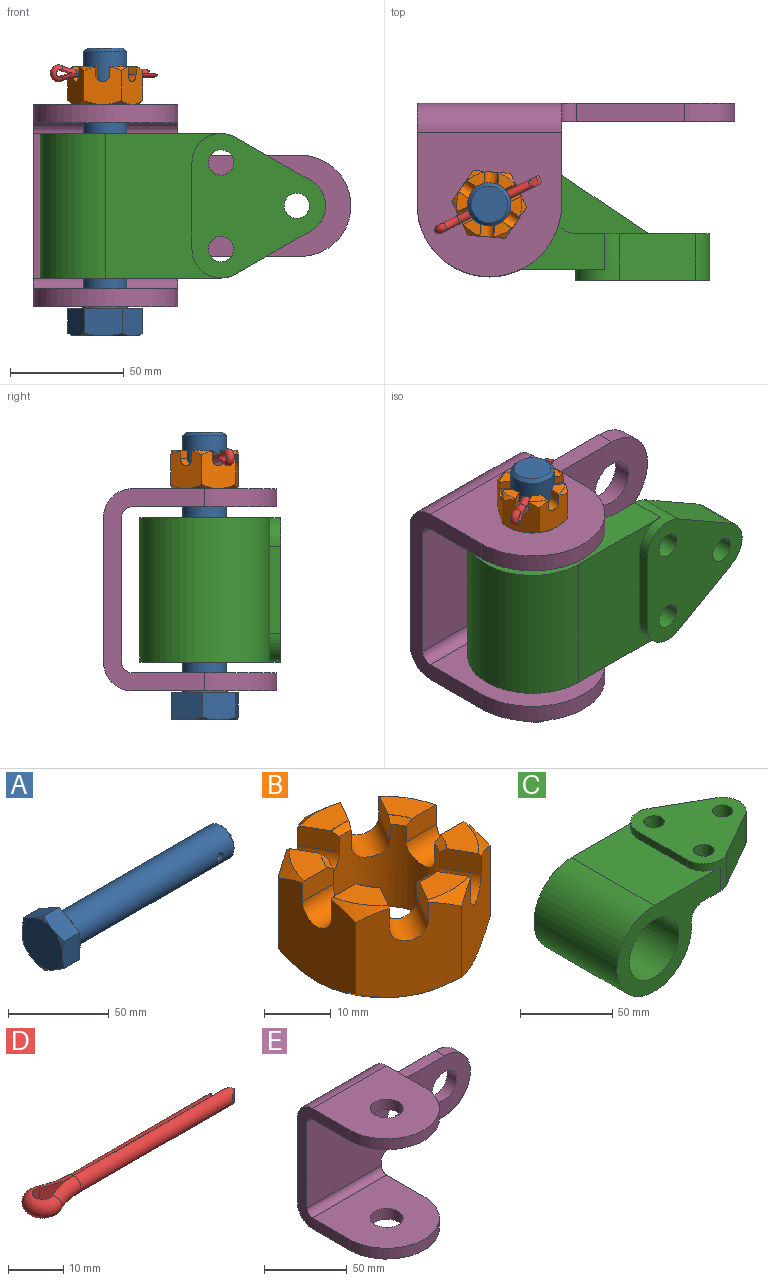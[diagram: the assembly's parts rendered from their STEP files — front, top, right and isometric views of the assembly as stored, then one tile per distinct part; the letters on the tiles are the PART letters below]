
ASSEMBLY  parts=5 mates=4
PART A: 26 faces, bbox 126.6x33x33 mm
  f0: plane 28.58x28.58mm, normal (1,0,0), area 325.1mm2, adj f10,f24
  f1: cylinder r=9.53mm len=112.28mm, axis (-1,0,0), area 6683.8mm2, adj f2,f24,f25
  f2: cone r=8.01mm half-angle=45deg, axis (-1,0,0), area 117.9mm2, adj f1,f3
  f3: plane 16.03x16.03mm, normal (1,0,0), area 201.7mm2, adj f2
  f4: plane 12.37x7.14mm, normal (1,0,0), area 11mm2, adj f10,f18,f23
  f5: plane 14.29x4.12mm, normal (1,0,0), area 11mm2, adj f10,f22,f23
  f6: plane 12.37x7.14mm, normal (1,0,0), area 11mm2, adj f10,f21,f22
  f7: plane 12.37x7.14mm, normal (1,0,0), area 11mm2, adj f10,f20,f21
  f8: plane 14.29x4.12mm, normal (1,0,0), area 11mm2, adj f10,f19,f20
  f9: plane 12.37x7.14mm, normal (1,0,0), area 11mm2, adj f10,f18,f19
  f10: cylinder r=14.29mm len=28.58mm, axis (-1,0,0), area 34.2mm2, adj f0,f4,f5,f6,f7,f8,f9
  f11: plane 28.58x28.58mm, normal (-1,0,0), area 641.3mm2, adj f12,f13,f14,f15,f16,f17
  f12: cone r=14.29mm half-angle=60deg, axis (1,0,0), area 12.7mm2, adj f11,f22,f23
  f13: cone r=14.29mm half-angle=60deg, axis (1,0,0), area 12.7mm2, adj f11,f21,f22
  f14: cone r=14.29mm half-angle=60deg, axis (1,0,0), area 12.7mm2, adj f11,f20,f21
  f15: cone r=14.29mm half-angle=60deg, axis (1,0,0), area 12.7mm2, adj f11,f19,f20
  f16: cone r=14.29mm half-angle=60deg, axis (1,0,0), area 12.7mm2, adj f11,f18,f23
  f17: cone r=14.29mm half-angle=60deg, axis (1,0,0), area 12.7mm2, adj f11,f18,f19
  f18: plane 16.51x11.89mm, normal (0,1,0), area 188.9mm2, adj f4,f9,f16,f17,f19,f23
  f19: plane 14.29x11.89mm, normal (0,0.5,-0.87), area 188.9mm2, adj f8,f9,f15,f17,f18,f20
  f20: plane 14.29x11.89mm, normal (0,-0.5,-0.87), area 188.9mm2, adj f7,f8,f14,f15,f19,f21
  f21: plane 16.51x11.89mm, normal (0,-1,0), area 188.9mm2, adj f6,f7,f13,f14,f20,f22
  f22: plane 14.29x11.89mm, normal (0,-0.5,0.87), area 188.9mm2, adj f5,f6,f12,f13,f21,f23
  f23: plane 14.29x11.89mm, normal (0,0.5,0.87), area 188.9mm2, adj f4,f5,f12,f16,f18,f22
  f24: torus R=10.03mm, axis (1,0,0), area 48.7mm2, adj f0,f1
  f25: cylinder r=2.38mm len=19.05mm, axis (0,-1,0), area 285mm2, adj f1
PART B: 64 faces, bbox 33x33x16.9 mm
  f0: cylinder r=8.33mm len=16.67mm, axis (0,0,1), area 599.6mm2, adj f8,f9,f10,f11,f12,f13,f14,f15
  f1: plane 28.58x28.58mm, normal (0,0,-1), area 356.3mm2, adj f32,f33,f34,f35,f36,f37,f51
  f2: plane 8.68x4.95mm, normal (0,0,1), area 30mm2, adj f12,f16,f41,f48
  f3: plane 7.52x6.81mm, normal (0,0,1), area 30mm2, adj f9,f13,f43,f49
  f4: plane 7.52x6.81mm, normal (0,0,1), area 30mm2, adj f8,f18,f39,f44
  f5: plane 7.52x6.81mm, normal (0,0,1), area 30mm2, adj f11,f15,f42,f46
  f6: plane 7.52x6.81mm, normal (0,0,1), area 30mm2, adj f10,f17,f40,f47
  f7: plane 8.68x4.95mm, normal (0,0,1), area 30mm2, adj f14,f19,f38,f45
  f8: plane 6.56x3.71mm, normal (0,-1,0), area 23.4mm2, adj f0,f4,f22,f26,f39,f44,f62,f63
  f9: plane 6.56x3.71mm, normal (0,1,0), area 23.4mm2, adj f0,f3,f22,f26,f43,f49,f52,f53
  f10: plane 6.56x3.71mm, normal (0,1,0), area 23.4mm2, adj f0,f6,f25,f27,f40,f47,f56,f57
  f11: plane 6.56x3.71mm, normal (0,-1,0), area 23.4mm2, adj f0,f5,f25,f27,f42,f46,f58,f59
  f12: plane 5.69x3.71mm, normal (0.87,0.5,0), area 23.4mm2, adj f0,f2,f23,f28,f41,f48,f54,f55
  f13: plane 5.69x3.71mm, normal (-0.87,-0.5,0), area 23.4mm2, adj f0,f3,f23,f28,f43,f49,f52,f53
  f14: plane 5.69x3.71mm, normal (-0.87,-0.5,0), area 23.4mm2, adj f0,f7,f20,f29,f38,f45,f60,f61
  f15: plane 5.69x3.71mm, normal (0.87,0.5,0), area 23.4mm2, adj f0,f5,f20,f29,f42,f46,f58,f59
  f16: plane 5.69x3.71mm, normal (-0.87,0.5,0), area 23.4mm2, adj f0,f2,f24,f30,f41,f48,f54,f55
  f17: plane 5.69x3.71mm, normal (0.87,-0.5,0), area 23.4mm2, adj f0,f6,f24,f30,f40,f47,f56,f57
  f18: plane 5.69x3.71mm, normal (-0.87,0.5,0), area 23.4mm2, adj f0,f4,f21,f31,f39,f44,f62,f63
  f19: plane 5.69x3.71mm, normal (0.87,-0.5,0), area 23.4mm2, adj f0,f7,f21,f31,f38,f45,f60,f61
  f20: plane 16.62x14.29mm, normal (-0.5,0.87,0), area 220.6mm2, adj f14,f15,f21,f25,f29,f32,f33,f38
  f21: plane 16.62x14.29mm, normal (0.5,0.87,0), area 220.6mm2, adj f18,f19,f20,f22,f31,f33,f34,f38
  f22: plane 16.63x16.51mm, normal (1,0,0), area 220.6mm2, adj f8,f9,f21,f23,f26,f34,f35,f39
  f23: plane 16.62x14.29mm, normal (0.5,-0.87,0), area 220.6mm2, adj f12,f13,f22,f24,f28,f35,f36,f41
  f24: plane 16.62x14.29mm, normal (-0.5,-0.87,0), area 220.6mm2, adj f16,f17,f23,f25,f30,f36,f37,f40
  f25: plane 16.63x16.51mm, normal (-1,0,0), area 220.6mm2, adj f10,f11,f20,f24,f27,f32,f37,f40
  f26: cylinder r=3.05mm len=6.53mm, axis (1,0,0), area 59.8mm2, adj f0,f8,f9,f22
  f27: cylinder r=3.05mm len=6.53mm, axis (1,0,0), area 59.8mm2, adj f0,f10,f11,f25
  f28: cylinder r=3.05mm len=8.7mm, axis (-0.5,0.87,0), area 59.8mm2, adj f0,f12,f13,f23
  f29: cylinder r=3.05mm len=8.7mm, axis (-0.5,0.87,0), area 59.8mm2, adj f0,f14,f15,f20
  f30: cylinder r=3.05mm len=8.7mm, axis (0.5,0.87,0), area 59.8mm2, adj f0,f16,f17,f24
  f31: cylinder r=3.05mm len=8.7mm, axis (0.5,0.87,0), area 59.8mm2, adj f0,f18,f19,f21
  f32: cone r=14.29mm half-angle=49.2deg, axis (0,0,1), area 14.5mm2, adj f1,f20,f25
  f33: cone r=14.29mm half-angle=49.2deg, axis (0,0,1), area 14.5mm2, adj f1,f20,f21
  f34: cone r=14.29mm half-angle=49.2deg, axis (0,0,1), area 14.5mm2, adj f1,f21,f22
  f35: cone r=14.29mm half-angle=49.2deg, axis (0,0,1), area 14.5mm2, adj f1,f22,f23
  f36: cone r=14.29mm half-angle=49.2deg, axis (0,0,1), area 14.5mm2, adj f1,f23,f24
  f37: cone r=14.29mm half-angle=49.2deg, axis (0,0,1), area 14.5mm2, adj f1,f24,f25
  f38: cone r=14.29mm half-angle=49.2deg, axis (0,0,-1), area 13.6mm2, adj f7,f14,f19,f20,f21
  f39: cone r=14.29mm half-angle=49.2deg, axis (0,0,-1), area 13.6mm2, adj f4,f8,f18,f21,f22
  f40: cone r=14.29mm half-angle=49.2deg, axis (0,0,-1), area 13.6mm2, adj f6,f10,f17,f24,f25
  f41: cone r=14.29mm half-angle=49.2deg, axis (0,0,-1), area 13.6mm2, adj f2,f12,f16,f23,f24
  f42: cone r=14.29mm half-angle=49.2deg, axis (0,0,-1), area 13.6mm2, adj f5,f11,f15,f20,f25
  f43: cone r=14.29mm half-angle=49.2deg, axis (0,0,-1), area 13.6mm2, adj f3,f9,f13,f22,f23
  f44: cone r=8.21mm half-angle=55deg, axis (0,0,1), area 0.1mm2, adj f4,f8,f18,f63
  f45: cone r=8.21mm half-angle=55deg, axis (0,0,1), area 0.1mm2, adj f7,f14,f19,f60
  f46: cone r=8.21mm half-angle=55deg, axis (0,0,1), area 0.1mm2, adj f5,f11,f15,f58
  f47: cone r=8.21mm half-angle=55deg, axis (0,0,1), area 0.1mm2, adj f6,f10,f17,f56
  f48: cone r=8.21mm half-angle=55deg, axis (0,0,1), area 0.1mm2, adj f2,f12,f16,f54
  f49: cone r=8.21mm half-angle=55deg, axis (0,0,1), area 0.1mm2, adj f3,f9,f13,f52
  f50: cone r=9.53mm half-angle=55deg, axis (0,0,-1), area 81.6mm2, adj f0,f51
  f51: cylinder r=9.53mm len=19.05mm, axis (0,0,1), area 1.5mm2, adj f1,f50
  f52: cone r=9.53mm half-angle=55deg, axis (0,0,-1), area 0.1mm2, adj f9,f13,f49,f53
  f53: cone r=8.33mm half-angle=55deg, axis (0,0,1), area 4.5mm2, adj f0,f9,f13,f52
  f54: cone r=9.53mm half-angle=55deg, axis (0,0,-1), area 0.1mm2, adj f12,f16,f48,f55
  f55: cone r=8.33mm half-angle=55deg, axis (0,0,1), area 4.5mm2, adj f0,f12,f16,f54
  f56: cone r=9.53mm half-angle=55deg, axis (0,0,-1), area 0.1mm2, adj f10,f17,f47,f57
  f57: cone r=8.33mm half-angle=55deg, axis (0,0,1), area 4.5mm2, adj f0,f10,f17,f56
  f58: cone r=9.53mm half-angle=55deg, axis (0,0,-1), area 0.1mm2, adj f11,f15,f46,f59
  f59: cone r=8.33mm half-angle=55deg, axis (0,0,1), area 4.5mm2, adj f0,f11,f15,f58
  f60: cone r=9.53mm half-angle=55deg, axis (0,0,-1), area 0.1mm2, adj f14,f19,f45,f61
  f61: cone r=8.33mm half-angle=55deg, axis (0,0,1), area 4.5mm2, adj f0,f14,f19,f60
  f62: cone r=8.33mm half-angle=55deg, axis (0,0,1), area 4.5mm2, adj f0,f8,f18,f63
  f63: cone r=9.53mm half-angle=55deg, axis (0,0,-1), area 0.1mm2, adj f8,f18,f44,f62
PART C: 21 faces, bbox 125.4x63.5x61.9 mm
  f0: cylinder r=9.53mm len=26.99mm, axis (0,-1,0), area 425.2mm2, adj f2,f4,f7,f9
  f1: plane 63.5x50.8mm, normal (0,0,1), area 2488.6mm2, adj f2,f6,f7,f11,f14,f15
  f2: cylinder r=28.57mm len=63.5mm, axis (0,-1,0), area 8413.5mm2, adj f0,f1,f3,f6,f7,f8,f9,f10
  f3: cylinder r=9.53mm len=26.99mm, axis (0,-1,0), area 425.2mm2, adj f2,f4,f6,f10
  f4: plane 63.5x58.88mm, normal (0,0,-1), area 2083.8mm2, adj f0,f3,f6,f7,f8,f9,f10,f12
  f5: cylinder r=19.05mm len=63.5mm, axis (0,-1,0), area 7600.6mm2, adj f6,f7
  f6: plane 79.38x57.15mm, normal (0,1,0), area 1971.2mm2, adj f1,f2,f3,f4,f5,f14
  f7: plane 79.38x57.15mm, normal (0,-1,0), area 1971.2mm2, adj f0,f1,f2,f4,f5,f15
  f8: plane 53.86x36.38mm, normal (0.56,0,-0.83), area 619mm2, adj f2,f4,f9,f10
  f9: plane 53.86x36.38mm, normal (0,-1,0), area 592.4mm2, adj f0,f2,f4,f8
  f10: plane 53.86x36.38mm, normal (0,1,0), area 592.4mm2, adj f2,f3,f4,f8
  f11: plane 38.1x4.78mm, normal (-1,0,0), area 181.9mm2, adj f1,f14,f15,f20
  f12: cylinder r=5.56mm len=20.65mm, axis (0,0,1), area 721.7mm2, adj f4,f20
  f13: cylinder r=5.56mm len=20.65mm, axis (0,0,1), area 721.7mm2, adj f4,f20
  f14: cylinder r=12.7mm len=20.65mm, axis (0,0,1), area 231.4mm2, adj f1,f4,f6,f11,f18,f20
  f15: cylinder r=12.7mm len=20.65mm, axis (0,0,1), area 231.4mm2, adj f1,f4,f7,f11,f16,f20
  f16: plane 33.35x20.65mm, normal (0.5,-0.87,0), area 793.1mm2, adj f4,f15,f17,f20
  f17: cylinder r=12.7mm len=22.06mm, axis (0,0,1), area 551.7mm2, adj f4,f16,f18,f20
  f18: plane 33.35x20.65mm, normal (0.5,0.87,0), area 793.1mm2, adj f4,f14,f17,f20
  f19: cylinder r=5.56mm len=20.65mm, axis (0,0,1), area 721.7mm2, adj f4,f20
  f20: plane 63.5x58.75mm, normal (0,0,1), area 2309.8mm2, adj f11,f12,f13,f14,f15,f16,f17,f18
PART D: 14 faces, bbox 52x8x3.7 mm
  f0: plane 38.67x3.7mm, normal (0,1,0), area 143.1mm2, adj f1,f2,f13
  f1: cylinder r=1.85mm len=40mm, axis (1,0,0), area 227.7mm2, adj f0,f3,f12,f13
  f2: cylinder r=16.37mm len=7.19mm, axis (0,0,-1), area 27.5mm2, adj f0,f3,f4
  f3: torus R=16.37mm, axis (0,0,-1), area 40.1mm2, adj f1,f2,f5
  f4: cylinder r=1.85mm len=3.7mm, axis (0,0,1), area 27.8mm2, adj f2,f5,f6
  f5: torus R=1.85mm, axis (0,0,1), area 71.2mm2, adj f3,f4,f7
  f6: cylinder r=16.37mm len=7.19mm, axis (0,0,-1), area 27.5mm2, adj f4,f7,f9
  f7: torus R=16.37mm, axis (0,0,-1), area 40.1mm2, adj f5,f6,f8
  f8: cylinder r=1.85mm len=36mm, axis (1,0,0), area 204.5mm2, adj f7,f9,f10,f11
  f9: plane 34.67x3.7mm, normal (0,-1,0), area 128.3mm2, adj f6,f8,f10
  f10: plane 3.7x1.33mm, normal (0.57,-0.82,0), area 5.7mm2, adj f8,f9,f11
  f11: plane 3.2x1.31mm, normal (0.58,0.82,0), area 3.6mm2, adj f8,f10
  f12: plane 3.2x1.31mm, normal (0.58,-0.82,0), area 3.6mm2, adj f1,f13
  f13: plane 3.7x1.33mm, normal (0.57,0.82,0), area 5.7mm2, adj f0,f1,f12
PART E: 24 faces, bbox 139.7x76.2x88.9 mm
  f0: plane 44.45x15.88mm, normal (1,0,0), area 386.1mm2, adj f9,f10,f11,f12,f13,f19,f21,f22
  f1: plane 88.9x44.45mm, normal (-1,0,0), area 1225.8mm2, adj f10,f11,f12,f13,f14,f15,f17,f19
  f2: plane 44.45x15.88mm, normal (1,0,0), area 386.1mm2, adj f3,f10,f11,f14,f15,f17,f20,f23
  f3: cylinder r=6.35mm len=7.94mm, axis (0,1,0), area 79.2mm2, adj f2,f4,f10,f11
  f4: plane 47.63x7.94mm, normal (0,0,-1), area 378mm2, adj f3,f5,f10,f11
  f5: cylinder r=22.23mm len=44.45mm, axis (0,1,0), area 554.2mm2, adj f4,f6,f10,f11
  f6: plane 47.63x7.94mm, normal (0,0,1), area 378mm2, adj f5,f9,f10,f11
  f7: cylinder r=10.33mm len=20.65mm, axis (0,1,0), area 514.9mm2, adj f10,f11
  f8: cylinder r=10.33mm len=20.65mm, axis (0,1,0), area 514.9mm2, adj f10,f11
  f9: cylinder r=6.35mm len=7.94mm, axis (0,1,0), area 79.2mm2, adj f0,f6,f10,f11
  f10: plane 139.7x63.5mm, normal (0,-1,0), area 6554.8mm2, adj f0,f1,f2,f3,f4,f5,f6,f7
  f11: plane 139.7x63.5mm, normal (0,1,0), area 6554.8mm2, adj f0,f1,f2,f3,f4,f5,f6,f7
  f12: plane 63.5x63.5mm, normal (0,0,-1), area 3290.3mm2, adj f0,f1,f18,f19,f21
  f13: plane 63.5x63.5mm, normal (0,0,1), area 3290.3mm2, adj f0,f1,f18,f19,f22
  f14: plane 63.5x63.5mm, normal (0,0,1), area 3290.3mm2, adj f1,f2,f16,f17,f20
  f15: plane 63.5x63.5mm, normal (0,0,-1), area 3290.3mm2, adj f1,f2,f16,f17,f23
  f16: cylinder r=9.92mm len=19.85mm, axis (0,0,-1), area 494.9mm2, adj f14,f15
  f17: cylinder r=31.75mm len=63.5mm, axis (0,0,-1), area 791.7mm2, adj f1,f2,f14,f15
  f18: cylinder r=9.92mm len=19.85mm, axis (0,0,-1), area 494.9mm2, adj f12,f13
  f19: cylinder r=31.75mm len=63.5mm, axis (0,0,1), area 791.7mm2, adj f0,f1,f12,f13
  f20: cylinder r=4.76mm len=63.5mm, axis (-1,0,0), area 475mm2, adj f1,f2,f10,f14
  f21: cylinder r=4.76mm len=63.5mm, axis (1,0,0), area 475mm2, adj f0,f1,f10,f12
  f22: cylinder r=12.7mm len=63.5mm, axis (-1,0,0), area 1266.8mm2, adj f0,f1,f11,f13
  f23: cylinder r=12.7mm len=63.5mm, axis (1,0,0), area 1266.8mm2, adj f1,f2,f11,f15
PLACE A rot(axis=(-0.47,-0.75,-0.47),106deg) t=(34.81,-42.55,-14.39)mm
PLACE B rot(axis=(0,0,-1),154.6deg) t=(34.81,-42.55,104.17)mm
PLACE C rot(axis=(1,0,0),90deg) t=(34.81,-42.55,42.83)mm
PLACE D rot(axis=(0.95,0.22,0.22),93deg) t=(14.22,-52.86,101.06)mm
PLACE E t=(3.06,1.9,-1.62)mm fixed
MATE revolute A.f1 <-> E.f16  axis (0,0,-1) through (34.81,-42.55,-1.62)mm
MATE revolute C.f2 <-> E.f16  axis (0,0,-1) through (34.81,-42.55,42.83)mm
MATE revolute E.f19 <-> B.f0  axis (0,0,1) through (34.81,-42.55,87.28)mm
MATE slider D.f8 <-> A.f25  axis (0.89,0.45,0) through (37.56,-41.17,101.06)mm
